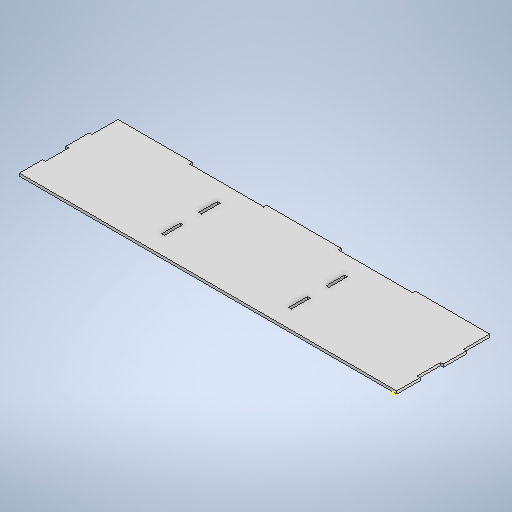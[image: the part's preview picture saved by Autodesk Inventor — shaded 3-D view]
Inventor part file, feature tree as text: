
AUTODESK INVENTOR PART (.ipt)
format: ipt  version: 2025.1 (Build 291241020, 241B)  size: 289,792 bytes
history: native  units: mm
features: sketch x2, extrude x1
ambient origin geometry x8: Origin, YZ Plane, XZ Plane, XY Plane, X Axis, Y Axis, Z Axis, Center Point
bodies: Solid1 (feature_tree)
feature tree (3):
  extrude  "Extrusion1"  Depth=100.0mm
  sketch  "Sketch2"  dims[d2=3.0mm d3=80.0mm d4=3.0mm d5=80.0mm d7=3.0mm d8=80.0mm d9=3.0mm d10=25.0mm d11=25.0mm d12=3.0mm d13=25.0mm d14=3.0mm d15=0.0mm d16=130.0mm d17=134.0mm d18=3.0mm d19=134.0mm d20=3.0mm d21=20.0mm d22=20.0mm d24=20.0mm]
  sketch  "Sketch1"  dims[d0=400.0mm d1=100.0mm]
